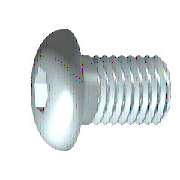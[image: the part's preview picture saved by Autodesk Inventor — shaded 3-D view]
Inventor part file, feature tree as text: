
AUTODESK INVENTOR PART (.ipt)
format: ipt  version: 2015 (Build 190159000, 159)  size: 196,096 bytes
history: native  units: mm (DEFAULTED — no unit token found)
features: sketch x2, other x1, extrude x1, plane x1
ambient origin geometry x7: Origin, YZ Plane, XY Plane, X Axis, Y Axis, Z Axis, Center Point
bodies: Body1 (feature_tree)
feature tree (5):
  other  "Bryła"
  extrude  "Szczelina"  Depth=18.0mm
  plane  "Work Plane1"
  sketch  "Szkic1"
  sketch  "Szkic2"
